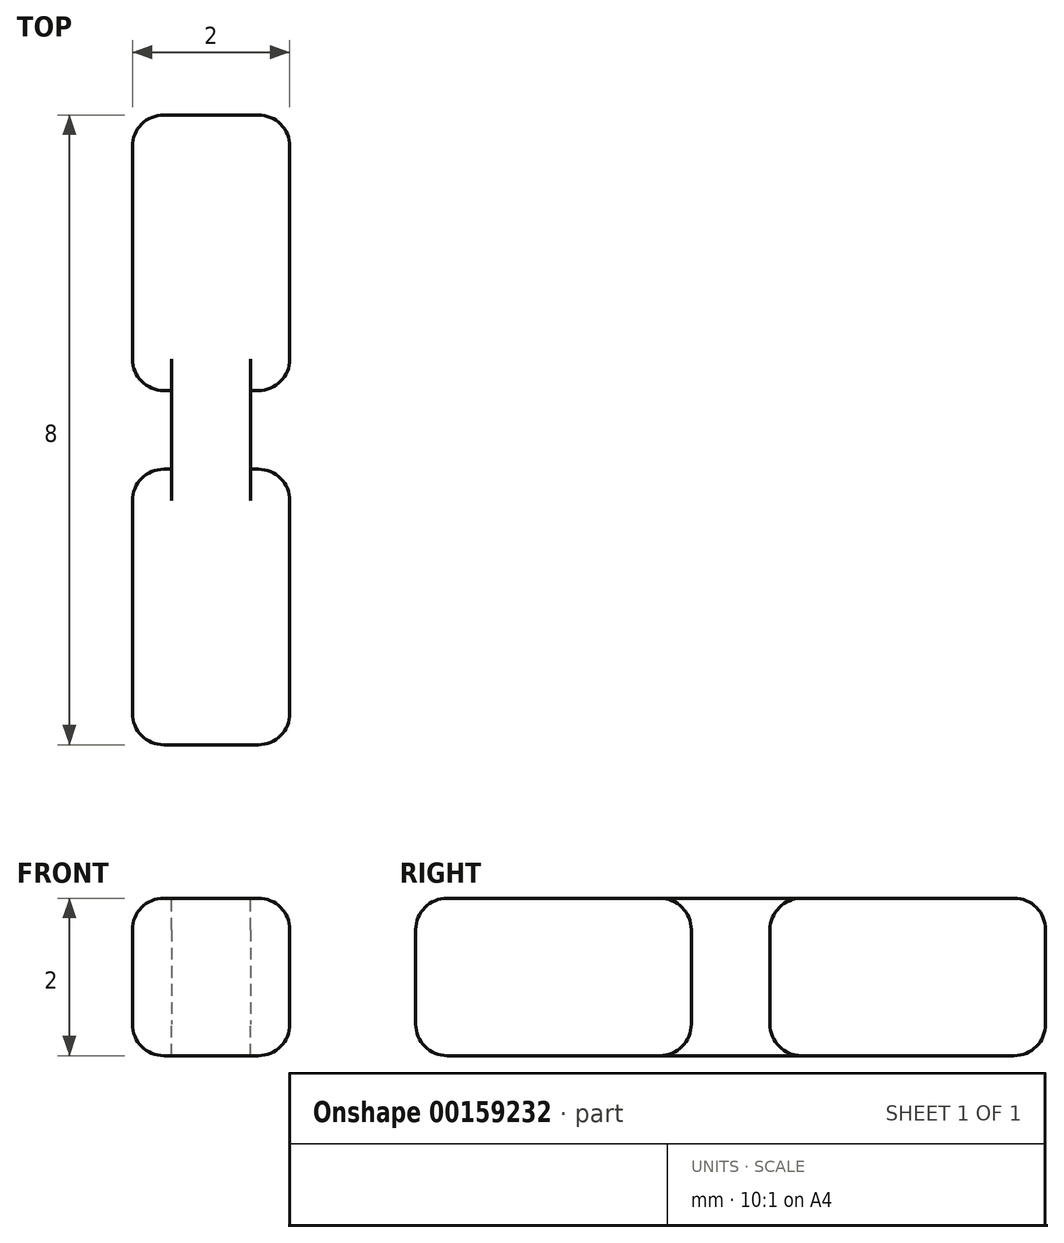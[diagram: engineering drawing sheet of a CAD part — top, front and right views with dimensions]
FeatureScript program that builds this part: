
annotation { "Feature Type Name" : "Feature", "Feature Type Description" : "" }
export const myFeature = defineFeature(function(context is Context, id is Id, definition is map)
    precondition{}
    {
        {
            var Q0;
            Q0=qCreatedBy(makeId("Top.planeOp"),FACE);
            var sketch = newSketch(context, id + "F0", { "sketchPlane" : qUnion([Q0])});
            skLineSegment(sketch, "E0.bottom", {"start": v(1, -4) * mm, "end": v(-1, -4) * mm});
            skLineSegment(sketch, "E0.top", {"start": v(1, 4) * mm, "end": v(-1, 4) * mm});
            skLineSegment(sketch, "E0.left", {"start": v(1, -4) * mm, "end": v(1, 4) * mm});
            skLineSegment(sketch, "E0.right", {"start": v(-1, -4) * mm, "end": v(-1, 4) * mm});
            skPoint(sketch, "E0.middle", {"position": v(0, 0) * mm});
            skLineSegment(sketch, "E1.bottom", {"start": v(-1, 0.5) * mm, "end": v(-0.5, 0.5) * mm});
            skLineSegment(sketch, "E1.top", {"start": v(-1, -0.5) * mm, "end": v(-0.5, -0.5) * mm});
            skLineSegment(sketch, "E1.left", {"start": v(-1, 0.5) * mm, "end": v(-1, -0.5) * mm});
            skLineSegment(sketch, "E1.right", {"start": v(-0.5, 0.5) * mm, "end": v(-0.5, -0.5) * mm});
            skLineSegment(sketch, "E2.bottom", {"start": v(1, -0.5) * mm, "end": v(0.5, -0.5) * mm});
            skLineSegment(sketch, "E2.top", {"start": v(1, 0.5) * mm, "end": v(0.5, 0.5) * mm});
            skLineSegment(sketch, "E2.left", {"start": v(1, -0.5) * mm, "end": v(1, 0.5) * mm});
            skLineSegment(sketch, "E2.right", {"start": v(0.5, -0.5) * mm, "end": v(0.5, 0.5) * mm});
            skLineSegment(sketch, "E3", {"start": v(-0.5, 0) * mm, "end": v(0.5, 0) * mm, "construction": true});
            skSolve(sketch);
        }
        {
            var Q0;
            {var subQ1=sQuery(id+"F0.wireOp",EDGE,"E0.bottom");Q0=makeQuery(id+"F0.imprint","IMPRINT",FACE,{"disambiguationData":[TD([[makeQuery(id+"F0.imprint","IMPRINT",EDGE,{"derivedFrom":subQ1}),-1.0]])]});}
            extrude(context, id + "F1", {"entities" : qUnion([Q0]), "depth" : 2 * mm});
        }
        {
            var Q0;
            Q0=makeQuery(id+"F1.opExtrude","CAP_EDGE",EDGE,{"disambiguationData":[OSD([sQuery(id+"F0.wireOp",EDGE,"E0.bottom")])],"isStart":false});
            var Q1;
            Q1=makeQuery(id+"F1.opExtrude","SWEPT_EDGE",EDGE,{"disambiguationData":[OSD([sQuery(id+"F0.wireOp",EDGE,"E0.bottom"),sQuery(id+"F0.wireOp",EDGE,"E0.left")])]});
            var Q2;
            Q2=makeQuery(id+"F1.opExtrude","SWEPT_EDGE",EDGE,{"disambiguationData":[OSD([sQuery(id+"F0.wireOp",EDGE,"E0.bottom"),sQuery(id+"F0.wireOp",EDGE,"E0.right")])]});
            var Q3;
            Q3=makeQuery(id+"F1.opExtrude","CAP_EDGE",EDGE,{"disambiguationData":[OSD([sQuery(id+"F0.wireOp",EDGE,"E0.bottom")])],"isStart":true});
            var Q4;
            Q4=makeQuery(id+"F1.opExtrude","SWEPT_EDGE",EDGE,{"disambiguationData":[OSD([sQuery(id+"F0.wireOp",EDGE,"E0.top"),sQuery(id+"F0.wireOp",EDGE,"E0.left")])]});
            var Q5;
            Q5=makeQuery(id+"F1.opExtrude","CAP_EDGE",EDGE,{"disambiguationData":[OSD([sQuery(id+"F0.wireOp",EDGE,"E0.top")])],"isStart":false});
            var Q6;
            Q6=makeQuery(id+"F1.opExtrude","SWEPT_FACE",FACE,{"disambiguationData":[OSD([sQuery(id+"F0.wireOp",EDGE,"E0.top")])]});
            var Q7;
            Q7=makeQuery(id+"F1.opExtrude","SWEPT_EDGE",EDGE,{"disambiguationData":[OSD([sQuery(id+"F0.wireOp",EDGE,"E0.top"),sQuery(id+"F0.wireOp",EDGE,"E0.right")])]});
            var Q8;
            Q8=makeQuery(id+"F1.opExtrude","SWEPT_EDGE",EDGE,{"disambiguationData":[OSD([sQuery(id+"F0.wireOp",EDGE,"E0.left"),sQuery(id+"F0.wireOp",EDGE,"E2.top"),sQuery(id+"F0.wireOp",EDGE,"E2.left")])]});
            var Q9;
            Q9=makeQuery(id+"F1.opExtrude","SWEPT_EDGE",EDGE,{"disambiguationData":[OSD([sQuery(id+"F0.wireOp",EDGE,"E0.left"),sQuery(id+"F0.wireOp",EDGE,"E2.bottom"),sQuery(id+"F0.wireOp",EDGE,"E2.left")])]});
            var Q10;
            Q10=makeQuery(id+"F1.opExtrude","SWEPT_EDGE",EDGE,{"disambiguationData":[OSD([sQuery(id+"F0.wireOp",EDGE,"E0.right"),sQuery(id+"F0.wireOp",EDGE,"E1.bottom"),sQuery(id+"F0.wireOp",EDGE,"E1.left")])]});
            var Q11;
            Q11=makeQuery(id+"F1.opExtrude","SWEPT_EDGE",EDGE,{"disambiguationData":[OSD([sQuery(id+"F0.wireOp",EDGE,"E0.right"),sQuery(id+"F0.wireOp",EDGE,"E1.top"),sQuery(id+"F0.wireOp",EDGE,"E1.left")])]});
            fillet(context, id + "F2", {"entities" : qUnion([Q0, Q1, Q2, Q3, Q4, Q5, Q6, Q7, Q8, Q9, Q10, Q11]), "radius" : 0.4 * mm, "tangentPropagation" : true, "allowEdgeOverflow" : false});
        }
        {
            var Q0;
            {var subQ0=sQuery(id+"F0.wireOp",EDGE,"E0.left");Q0=makeQuery(id+"F1.opExtrude","CAP_EDGE",EDGE,{"disambiguationData":[OSD([subQ0]),TDD([makeQuery(id+"F0.imprint","IMPRINT",EDGE,{"disambiguationData":[TD([[makeQuery(id+"F0.imprint","INTERSECT",VERTEX,{"derivedFrom":[sQuery(id+"F0.wireOp",EDGE,"E0.bottom"),subQ0]}),-1.0]])],"derivedFrom":subQ0})])],"isStart":false});}
            var Q1;
            {var subQ0=sQuery(id+"F0.wireOp",EDGE,"E0.left");Q1=makeQuery(id+"F1.opExtrude","CAP_EDGE",EDGE,{"disambiguationData":[OSD([subQ0]),TDD([makeQuery(id+"F0.imprint","IMPRINT",EDGE,{"disambiguationData":[TD([[makeQuery(id+"F0.imprint","INTERSECT",VERTEX,{"derivedFrom":[sQuery(id+"F0.wireOp",EDGE,"E0.bottom"),subQ0]}),-1.0]])],"derivedFrom":subQ0})])],"isStart":true});}
            var Q2;
            {var subQ0=sQuery(id+"F0.wireOp",EDGE,"E0.left");Q2=makeQuery(id+"F1.opExtrude","CAP_EDGE",EDGE,{"disambiguationData":[OSD([subQ0]),TDD([makeQuery(id+"F0.imprint","IMPRINT",EDGE,{"disambiguationData":[TD([[makeQuery(id+"F0.imprint","INTERSECT",VERTEX,{"derivedFrom":[sQuery(id+"F0.wireOp",EDGE,"E0.top"),subQ0]}),1.0]])],"derivedFrom":subQ0})])],"isStart":false});}
            var Q3;
            {var subQ0=sQuery(id+"F0.wireOp",EDGE,"E0.left");Q3=makeQuery(id+"F1.opExtrude","CAP_EDGE",EDGE,{"disambiguationData":[OSD([subQ0]),TDD([makeQuery(id+"F0.imprint","IMPRINT",EDGE,{"disambiguationData":[TD([[makeQuery(id+"F0.imprint","INTERSECT",VERTEX,{"derivedFrom":[sQuery(id+"F0.wireOp",EDGE,"E0.top"),subQ0]}),1.0]])],"derivedFrom":subQ0})])],"isStart":true});}
            var Q4;
            {var subQ0=sQuery(id+"F0.wireOp",EDGE,"E0.right");Q4=makeQuery(id+"F1.opExtrude","CAP_EDGE",EDGE,{"disambiguationData":[OSD([subQ0]),TDD([makeQuery(id+"F0.imprint","IMPRINT",EDGE,{"disambiguationData":[TD([[makeQuery(id+"F0.imprint","INTERSECT",VERTEX,{"derivedFrom":[sQuery(id+"F0.wireOp",EDGE,"E0.bottom"),subQ0]}),-1.0]])],"derivedFrom":subQ0})])],"isStart":false});}
            var Q5;
            {var subQ0=sQuery(id+"F0.wireOp",EDGE,"E0.right");Q5=makeQuery(id+"F1.opExtrude","CAP_EDGE",EDGE,{"disambiguationData":[OSD([subQ0]),TDD([makeQuery(id+"F0.imprint","IMPRINT",EDGE,{"disambiguationData":[TD([[makeQuery(id+"F0.imprint","INTERSECT",VERTEX,{"derivedFrom":[sQuery(id+"F0.wireOp",EDGE,"E0.top"),subQ0]}),1.0]])],"derivedFrom":subQ0})])],"isStart":false});}
            var Q6;
            {var subQ0=sQuery(id+"F0.wireOp",EDGE,"E0.right");Q6=makeQuery(id+"F1.opExtrude","CAP_EDGE",EDGE,{"disambiguationData":[OSD([subQ0]),TDD([makeQuery(id+"F0.imprint","IMPRINT",EDGE,{"disambiguationData":[TD([[makeQuery(id+"F0.imprint","INTERSECT",VERTEX,{"derivedFrom":[sQuery(id+"F0.wireOp",EDGE,"E0.bottom"),subQ0]}),-1.0]])],"derivedFrom":subQ0})])],"isStart":true});}
            var Q7;
            {var subQ0=sQuery(id+"F0.wireOp",EDGE,"E0.right");Q7=makeQuery(id+"F1.opExtrude","CAP_EDGE",EDGE,{"disambiguationData":[OSD([subQ0]),TDD([makeQuery(id+"F0.imprint","IMPRINT",EDGE,{"disambiguationData":[TD([[makeQuery(id+"F0.imprint","INTERSECT",VERTEX,{"derivedFrom":[sQuery(id+"F0.wireOp",EDGE,"E0.top"),subQ0]}),1.0]])],"derivedFrom":subQ0})])],"isStart":true});}
            fillet(context, id + "F3", {"entities" : qUnion([Q0, Q1, Q2, Q3, Q4, Q5, Q6, Q7]), "radius" : 0.4 * mm, "tangentPropagation" : true, "allowEdgeOverflow" : false});
        }
    });
